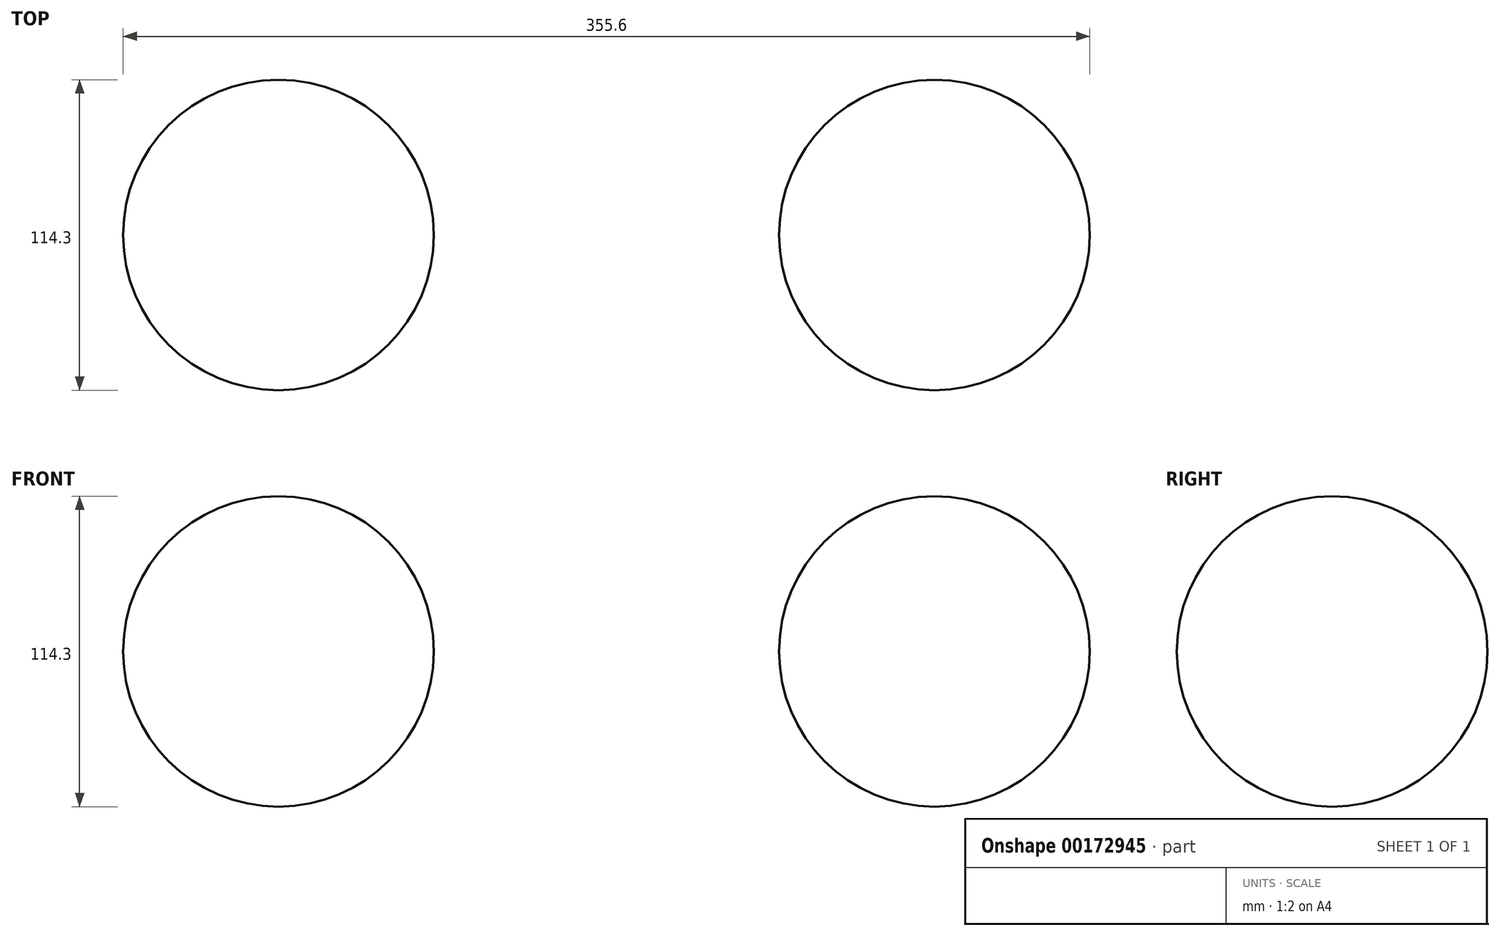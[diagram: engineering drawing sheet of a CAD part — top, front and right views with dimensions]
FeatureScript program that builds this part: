
annotation { "Feature Type Name" : "Feature", "Feature Type Description" : "" }
export const myFeature = defineFeature(function(context is Context, id is Id, definition is map)
    precondition{}
    {
        {
            var Q0;
            Q0=qCreatedBy(makeId("Front.planeOp"),FACE);
            var sketch = newSketch(context, id + "F0", { "sketchPlane" : qUnion([Q0])});
            skCircle(sketch, "E0", {"center": v(-120.65, 0) * mm, "radius": 57.15 * mm});
            skCircle(sketch, "E1", {"center": v(120.65, 0) * mm, "radius": 57.15 * mm});
            skSolve(sketch);
        }
        {
            var Q0;
            Q0=makeQuery(id+"F0.imprint","IMPRINT",FACE,{"disambiguationData":[TD([[makeQuery(id+"F0.imprint","IMPRINT",EDGE,{"derivedFrom":sQuery(id+"F0.wireOp",EDGE,"E1")}),1.0]])]});
            var Q1;
            Q1=makeQuery(id+"F0.imprint","IMPRINT",FACE,{"disambiguationData":[TD([[makeQuery(id+"F0.imprint","IMPRINT",EDGE,{"derivedFrom":sQuery(id+"F0.wireOp",EDGE,"E0")}),1.0]])]});
            extrude(context, id + "F1", {"entities" : qUnion([Q0, Q1]), "endBound" : BoundingType.SYMMETRIC, "depth" : 114.3 * mm});
        }
        {
            var Q0;
            Q0=makeQuery(id+"F1.opExtrude","CAP_EDGE",EDGE,{"disambiguationData":[OSD([sQuery(id+"F0.wireOp",EDGE,"E1")])],"isStart":true});
            var Q1;
            Q1=makeQuery(id+"F1.opExtrude","CAP_EDGE",EDGE,{"disambiguationData":[OSD([sQuery(id+"F0.wireOp",EDGE,"E1")])],"isStart":false});
            var Q2;
            Q2=makeQuery(id+"F1.opExtrude","CAP_EDGE",EDGE,{"disambiguationData":[OSD([sQuery(id+"F0.wireOp",EDGE,"E0")])],"isStart":false});
            var Q3;
            Q3=makeQuery(id+"F1.opExtrude","CAP_EDGE",EDGE,{"disambiguationData":[OSD([sQuery(id+"F0.wireOp",EDGE,"E0")])],"isStart":true});
            fillet(context, id + "F2", {"entities" : qUnion([Q0, Q1, Q2, Q3]), "radius" : 57.15 * mm, "tangentPropagation" : true, "allowEdgeOverflow" : false});
        }
    });
